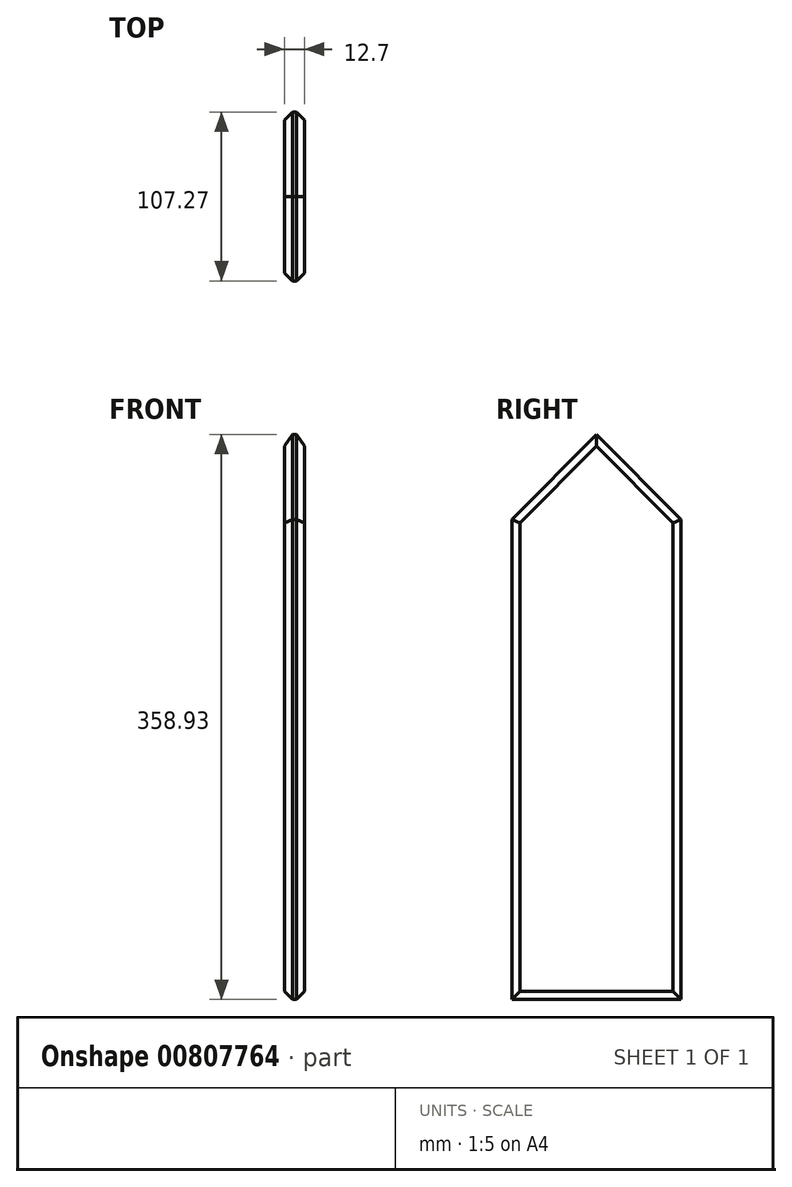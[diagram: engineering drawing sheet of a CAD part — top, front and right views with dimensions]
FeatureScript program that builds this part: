
annotation { "Feature Type Name" : "Feature", "Feature Type Description" : "" }
export const myFeature = defineFeature(function(context is Context, id is Id, definition is map)
    precondition{}
    {
        {
            var Q0;
            Q0=qCreatedBy(makeId("Right.planeOp"),FACE);
            var sketch = newSketch(context, id + "F0", { "sketchPlane" : qUnion([Q0])});
            skLineSegment(sketch, "E0", {"start": v(-107.27, -304.8) * mm, "end": v(-107.27, 0) * mm});
            skLineSegment(sketch, "E1", {"start": v(0, 0) * mm, "end": v(0, -304.8) * mm});
            skLineSegment(sketch, "E2", {"start": v(0, -304.8) * mm, "end": v(-107.27, -304.8) * mm});
            skLineSegment(sketch, "E3", {"start": v(-107.27, 0) * mm, "end": v(-53.63, 54.13) * mm});
            skLineSegment(sketch, "E4", {"start": v(-53.63, 54.13) * mm, "end": v(0, 0) * mm});
            skLineSegment(sketch, "E5", {"start": v(-53.63, 54.13) * mm, "end": v(-53.63, -266.03) * mm});
            skSolve(sketch);
        }
        {
            var Q0;
            Q0=makeQuery(id+"F0.imprint","IMPRINT",FACE,{"disambiguationData":[TD([[makeQuery(id+"F0.imprint","IMPRINT",EDGE,{"derivedFrom":sQuery(id+"F0.wireOp",EDGE,"E0")}),-1.0]])]});
            extrude(context, id + "F1", {"entities" : qUnion([Q0]), "depth" : 12.7 * mm, "offsetDistance" : 25.4 * mm});
        }
        {
            var Q0;
            Q0=makeQuery(id+"F1.opExtrude","CAP_FACE",FACE,{"disambiguationData":[OSD([sQuery(id+"F0.wireOp",EDGE,"E0"),sQuery(id+"F0.wireOp",EDGE,"E1"),sQuery(id+"F0.wireOp",EDGE,"E2"),sQuery(id+"F0.wireOp",EDGE,"E3"),sQuery(id+"F0.wireOp",EDGE,"E4")])],"isStart":false});
            var Q1;
            Q1=makeQuery(id+"F1.opExtrude","CAP_FACE",FACE,{"disambiguationData":[OSD([sQuery(id+"F0.wireOp",EDGE,"E0"),sQuery(id+"F0.wireOp",EDGE,"E1"),sQuery(id+"F0.wireOp",EDGE,"E2"),sQuery(id+"F0.wireOp",EDGE,"E3"),sQuery(id+"F0.wireOp",EDGE,"E4")])],"isStart":true});
            chamfer(context, id + "F2", {"entities" : qUnion([Q0, Q1]), "width" : 5.08 * mm, "tangentPropagation" : true});
        }
    });
